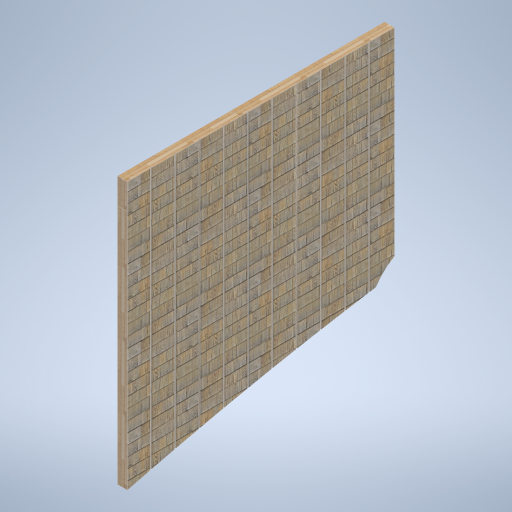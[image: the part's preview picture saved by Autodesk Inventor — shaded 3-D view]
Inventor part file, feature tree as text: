
AUTODESK INVENTOR PART (.ipt)
format: ipt  version: 2024.2 (Build 282272000, 272)  size: 504,832 bytes
history: native  units: in
note: dims shown in document units (in); Inventor stores cm internally (conversion verified against a paired STEP export)
features: other x3, sketch x2
ambient origin geometry x8: Origin, YZ Plane, XZ Plane, XY Plane, X Axis, Y Axis, Z Axis, Center Point
bodies: Solid1 (feature_tree)
feature tree (5):
  other  "side_wall_01.ipt"
  other  "Solid1::side_wall_01.ipt"
  other  "TaggingFeature1"
  sketch  "Sketch1"  dims[d0=0.3937in]
  sketch  "Sketch2"
